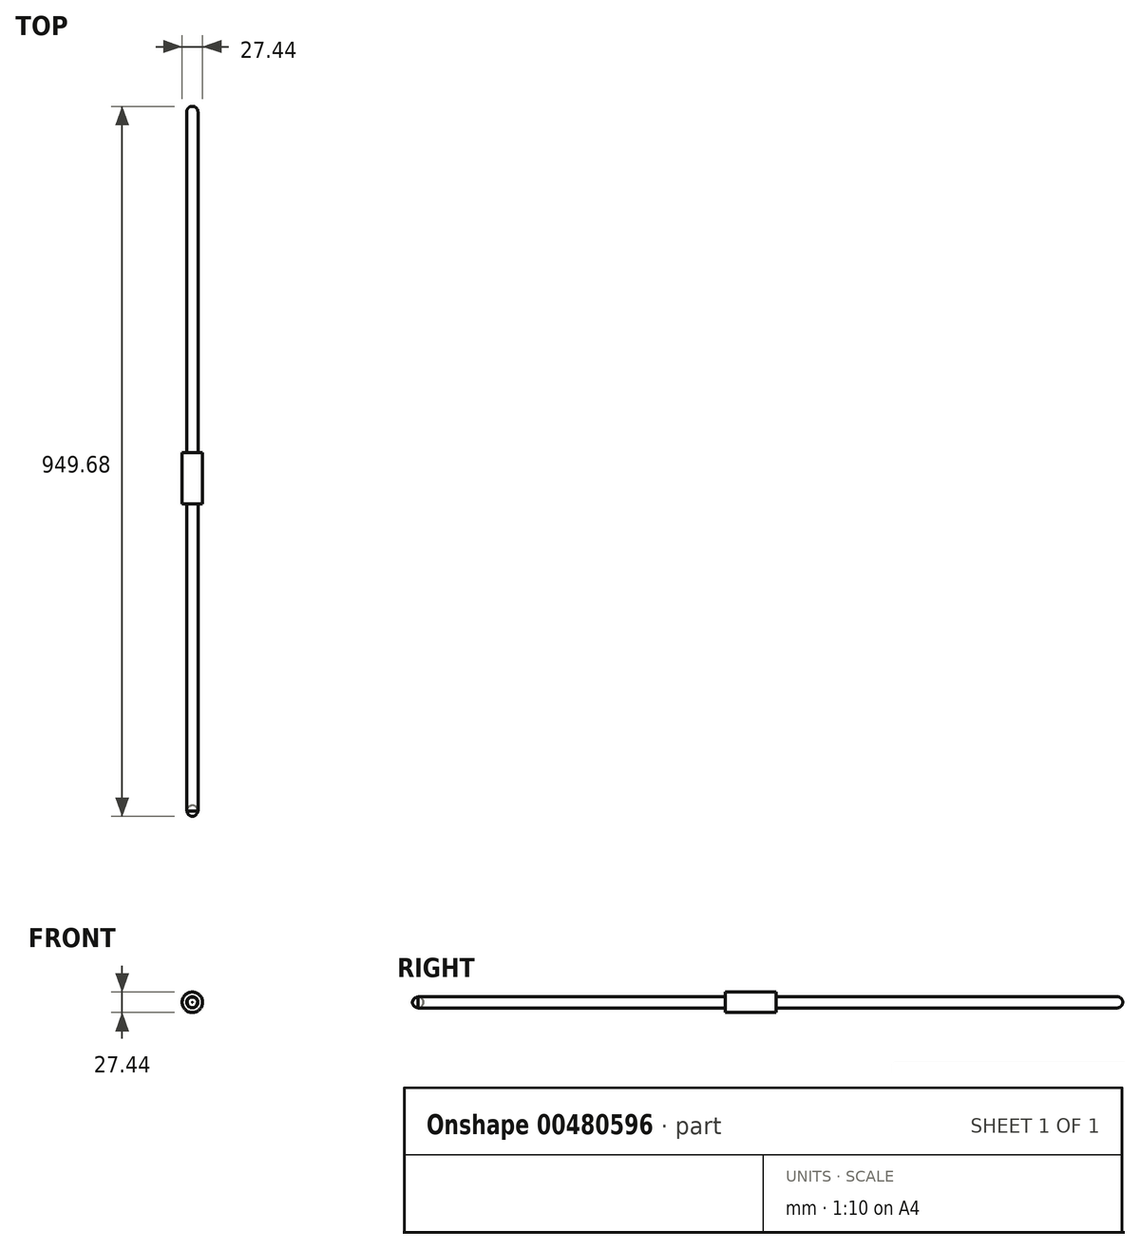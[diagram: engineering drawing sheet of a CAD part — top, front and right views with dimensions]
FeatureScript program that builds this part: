
annotation { "Feature Type Name" : "Feature", "Feature Type Description" : "" }
export const myFeature = defineFeature(function(context is Context, id is Id, definition is map)
    precondition{}
    {
        {
            var Q0;
            Q0=qCreatedBy(makeId("Top.planeOp"),FACE);
            var sketch = newSketch(context, id + "F0", { "sketchPlane" : qUnion([Q0])});
            skLineSegment(sketch, "E0.bottom", {"start": v(-13.72, 11.58) * mm, "end": v(0, 11.58) * mm});
            skLineSegment(sketch, "E0.top", {"start": v(-13.72, -56.66) * mm, "end": v(13.54, -56.66) * mm});
            skLineSegment(sketch, "E0.left", {"start": v(-13.72, 11.58) * mm, "end": v(-13.72, -56.66) * mm});
            skLineSegment(sketch, "E1.bottom", {"start": v(7.47, 474.84) * mm, "end": v(-7.47, 474.84) * mm});
            skLineSegment(sketch, "E1.top", {"start": v(0, -474.84) * mm, "end": v(-7.47, -474.84) * mm});
            skLineSegment(sketch, "E1.right", {"start": v(-7.47, 474.84) * mm, "end": v(-7.47, 11.58) * mm});
            skPoint(sketch, "E1.middle", {"position": v(0, 0) * mm});
            skLineSegment(sketch, "E2.trimOffspring", {"start": v(-7.47, -56.66) * mm, "end": v(-7.47, -474.84) * mm});
            skLineSegment(sketch, "E3", {"start": v(0, 474.84) * mm, "end": v(0, -474.84) * mm});
            skPoint(sketch, "E4.trimOffspring.end.orphan", {"position": v(7.47, -474.84) * mm});
            skSolve(sketch);
        }
        {
            var Q0;
            {var subQ4=sQuery(id+"F0.wireOp",EDGE,"E0.left");Q0=makeQuery(id+"F0.imprint","IMPRINT",FACE,{"disambiguationData":[TD([[makeQuery(id+"F0.imprint","IMPRINT",EDGE,{"derivedFrom":subQ4}),1.0]])]});}
            var Q1;
            {var subQ3=sQuery(id+"F0.wireOp",EDGE,"E1.right");Q1=makeQuery(id+"F0.imprint","IMPRINT",FACE,{"disambiguationData":[TD([[makeQuery(id+"F0.imprint","IMPRINT",EDGE,{"derivedFrom":subQ3}),1.0]])]});}
            var Q2;
            {var subQ4=sQuery(id+"F0.wireOp",EDGE,"E1.top");Q2=makeQuery(id+"F0.imprint","IMPRINT",FACE,{"disambiguationData":[TD([[makeQuery(id+"F0.imprint","IMPRINT",EDGE,{"derivedFrom":subQ4}),-1.0]])]});}
            var Q3;
            Q3=sQuery(id+"F0.wireOp",EDGE,"E3");
            revolve(context, id + "F1", {"entities" : qUnion([Q0, Q1, Q2]), "axis" : qUnion([Q3]), "revolveType" : RevolveType.FULL});
        }
        {
            var Q0;
            Q0=makeQuery(id+"F1.opRevolve","SWEPT_EDGE",EDGE,{"disambiguationData":[OSD([sQuery(id+"F0.wireOp",EDGE,"E1.bottom"),sQuery(id+"F0.wireOp",EDGE,"E1.right")])]});
            var Q1;
            Q1=makeQuery(id+"F1.opRevolve","SWEPT_EDGE",EDGE,{"disambiguationData":[OSD([sQuery(id+"F0.wireOp",EDGE,"E1.top"),sQuery(id+"F0.wireOp",EDGE,"E2.trimOffspring")])]});
            fillet(context, id + "F2", {"entities" : qUnion([Q0, Q1]), "radius" : 7.3 * mm, "tangentPropagation" : true, "allowEdgeOverflow" : false});
        }
    });
